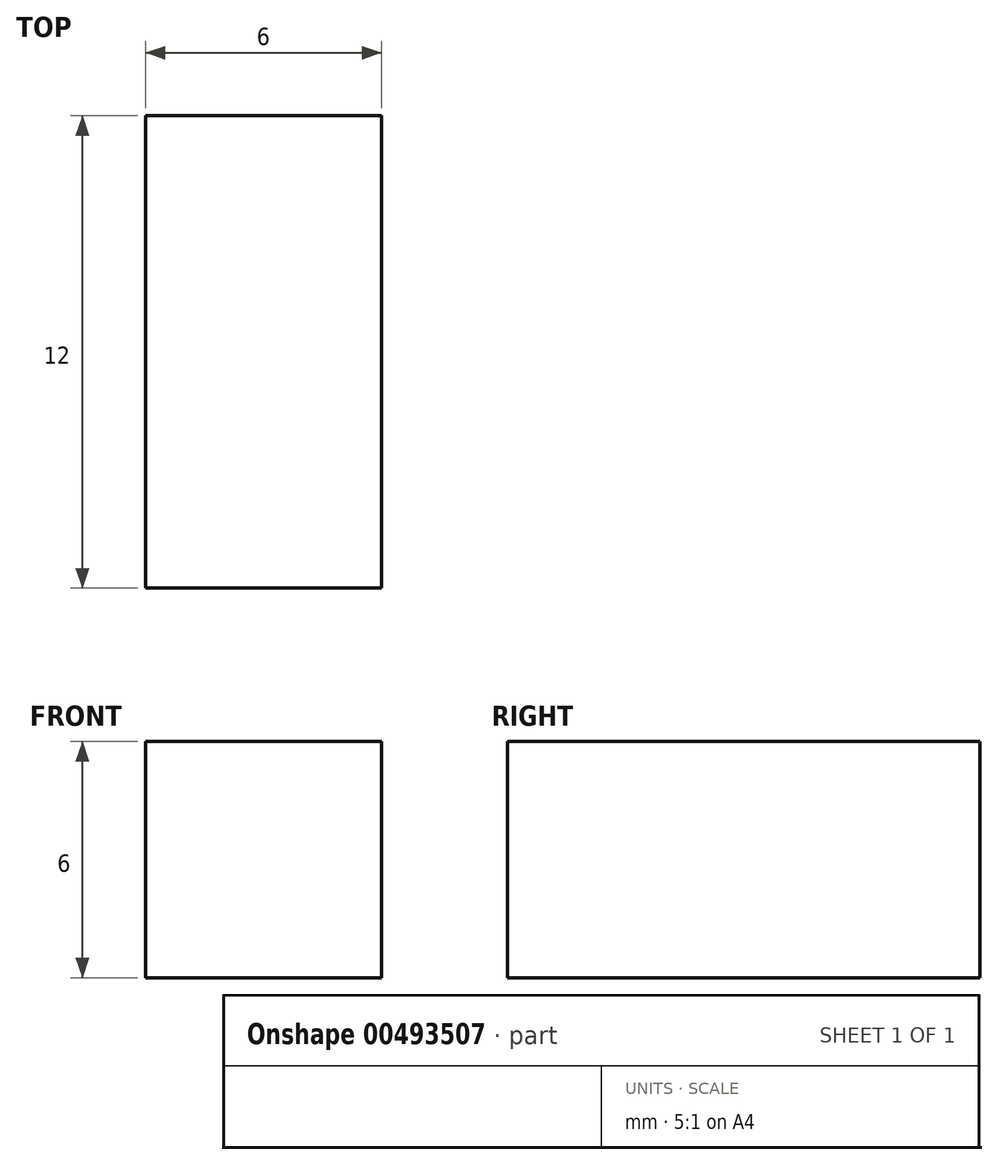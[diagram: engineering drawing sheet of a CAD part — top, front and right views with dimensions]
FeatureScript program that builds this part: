
annotation { "Feature Type Name" : "Feature", "Feature Type Description" : "" }
export const myFeature = defineFeature(function(context is Context, id is Id, definition is map)
    precondition{}
    {
        {
            var Q0;
            Q0=qCreatedBy(makeId("Front.planeOp"),FACE);
            var sketch = newSketch(context, id + "F0", { "sketchPlane" : qUnion([Q0])});
            skLineSegment(sketch, "E0.bottom", {"start": v(-3, 3) * mm, "end": v(3, 3) * mm});
            skLineSegment(sketch, "E0.top", {"start": v(-3, -3) * mm, "end": v(3, -3) * mm});
            skLineSegment(sketch, "E0.left", {"start": v(-3, 3) * mm, "end": v(-3, -3) * mm});
            skLineSegment(sketch, "E0.right", {"start": v(3, 3) * mm, "end": v(3, -3) * mm});
            skSolve(sketch);
        }
        {
            var Q0;
            Q0=makeQuery(id+"F0.imprint","IMPRINT",FACE,{"disambiguationData":[TD([[makeQuery(id+"F0.imprint","IMPRINT",EDGE,{"derivedFrom":sQuery(id+"F0.wireOp",EDGE,"E0.bottom")}),-1.0]])]});
            extrude(context, id + "F1", {"entities" : qUnion([Q0]), "depth" : 12 * mm, "offsetDistance" : 25 * mm});
        }
    });
